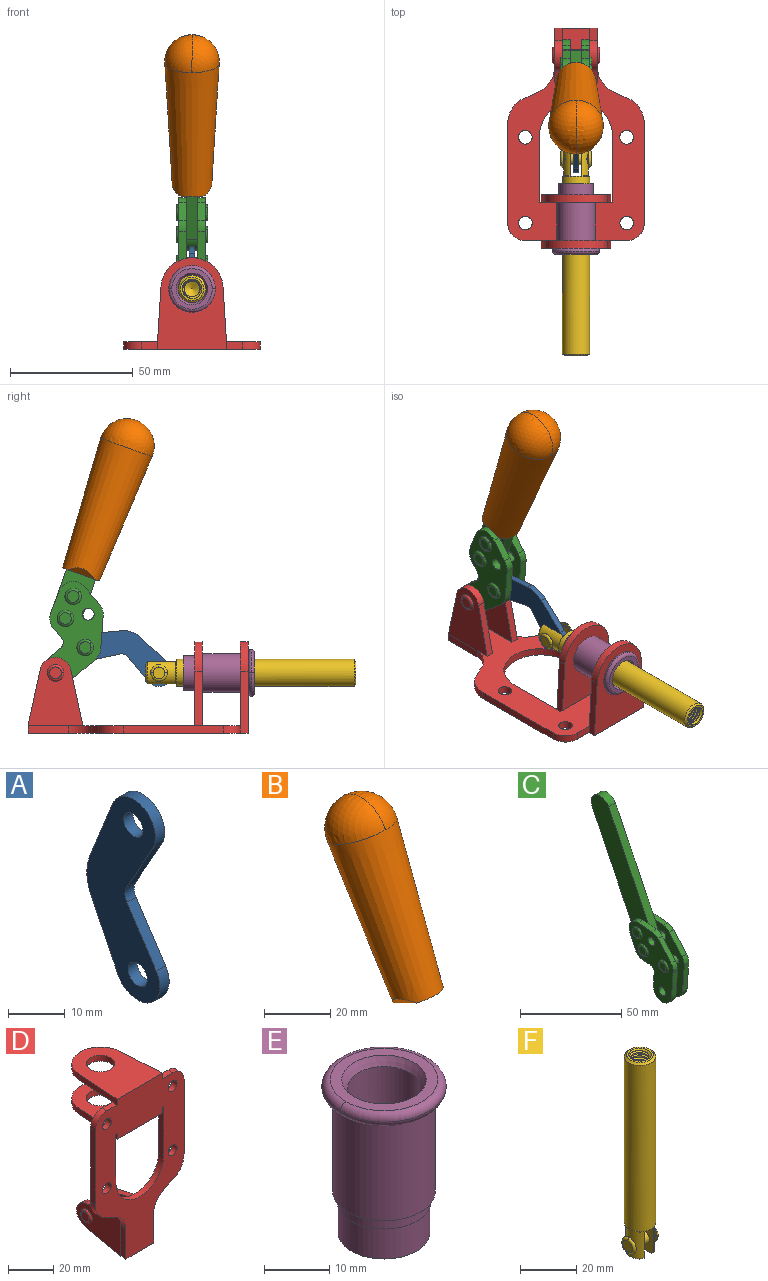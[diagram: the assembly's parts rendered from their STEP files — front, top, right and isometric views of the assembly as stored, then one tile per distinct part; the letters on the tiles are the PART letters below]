
ASSEMBLY  parts=6 mates=6
PART A: 12 faces, bbox 2.3x18.2x42.8 mm
  f0: cylinder r=2.4mm len=4.8mm, axis (1,0,0), area 34.9mm2, adj f4,f11
  f1: cylinder r=10.41mm len=8.47mm, axis (1,0,0), area 20.2mm2, adj f4,f9,f10,f11
  f2: cylinder r=3.05mm len=3.16mm, axis (1,0,0), area 7.7mm2, adj f4,f6,f7,f11
  f3: cylinder r=2.4mm len=4.8mm, axis (1,0,0), area 34.9mm2, adj f4,f11
  f4: plane 42.81x18.23mm, normal (-1,0,0), area 414.1mm2, adj f0,f1,f2,f3,f5,f6,f7,f8
  f5: cylinder r=5.54mm len=10.67mm, axis (1,0,0), area 41.8mm2, adj f4,f6,f10,f11
  f6: plane 11.66x6.53mm, normal (0,-0.87,-0.49), area 30.9mm2, adj f2,f4,f5,f11
  f7: plane 11.17x7.33mm, normal (0,-0.84,0.55), area 30.9mm2, adj f2,f4,f8,f11
  f8: cylinder r=5.54mm len=10.51mm, axis (1,0,0), area 41.8mm2, adj f4,f7,f9,f11
  f9: plane 13.67x6.67mm, normal (0,0.9,-0.44), area 35.1mm2, adj f1,f4,f8,f11
  f10: plane 14.1x5.7mm, normal (0,0.93,0.37), area 35.1mm2, adj f1,f4,f5,f11
  f11: plane 42.81x18.23mm, normal (1,0,0), area 414.1mm2, adj f0,f1,f2,f3,f5,f6,f7,f8
PART B: 11 faces, bbox 22.3x42.6x64.5 mm
  f0: sphere r=11.13mm, area 411.4mm2, adj f1,f8
  f1: cone r=11.11mm half-angle=3.3deg, axis (0,0.44,0.9), area 3251.8mm2, adj f0,f7,f8,f9,f10
  f2: cylinder r=6.16mm len=11.7mm, axis (1,0,0), area 89.5mm2, adj f3,f4,f5,f6
  f3: plane 60.23x36.75mm, normal (-1,0,0), area 763.6mm2, adj f2,f4,f6,f10
  f4: plane 51.37x25.05mm, normal (0,0.9,-0.44), area 264.2mm2, adj f2,f3,f5,f10
  f5: plane 60.23x36.75mm, normal (1,0,0), area 763.6mm2, adj f2,f4,f6,f10
  f6: plane 51.37x25.05mm, normal (0,-0.9,0.44), area 264.2mm2, adj f2,f3,f5,f10
  f7: plane 9.95x5.95mm, normal (0.71,-0.31,-0.64), area 25.8mm2, adj f1,f10
  f8: sphere r=11.13mm, area 411.4mm2, adj f0,f1
  f9: plane 9.95x5.95mm, normal (-0.71,-0.31,-0.64), area 25.8mm2, adj f1,f10
  f10: plane 14.27x11.38mm, normal (0,-0.44,-0.9), area 106.7mm2, adj f1,f3,f4,f5,f6,f7,f9
PART C: 59 faces, bbox 12.9x60.2x99.6 mm
  f0: torus R=2.39mm, axis (-1,0,0), area 14.9mm2, adj f20,f43,f51
  f1: torus R=2.39mm, axis (-1,0,0), area 14.9mm2, adj f19,f42,f51
  f2: torus R=2.39mm, axis (-1,0,0), area 14.9mm2, adj f18,f35,f51
  f3: torus R=2.39mm, axis (-1,0,0), area 14.9mm2, adj f14,f17,f23
  f4: torus R=2.39mm, axis (-1,0,0), area 14.9mm2, adj f13,f16,f23
  f5: torus R=2.39mm, axis (-1,0,0), area 14.9mm2, adj f12,f15,f23
  f6: cylinder r=2.39mm len=4.78mm, axis (1,0,0), area 46.5mm2, adj f48,f50,f51
  f7: cylinder r=2.39mm len=4.78mm, axis (1,0,0), area 46.5mm2, adj f50,f51
  f8: cylinder r=6.35mm len=12.68mm, axis (1,0,0), area 61.8mm2, adj f38,f39,f50,f51
  f9: cylinder r=2.39mm len=4.78mm, axis (-1,0,0), area 70.5mm2, adj f46,f50
  f10: cylinder r=2.39mm len=4.78mm, axis (-1,0,0), area 46.5mm2, adj f23,f45,f46
  f11: cylinder r=2.39mm len=4.78mm, axis (-1,0,0), area 46.5mm2, adj f23,f46
  f12: plane 4.78x4.78mm, normal (1,0,0), area 17.9mm2, adj f5,f15
  f13: plane 4.78x4.78mm, normal (1,0,0), area 17.9mm2, adj f4,f16
  f14: plane 4.78x4.78mm, normal (1,0,0), area 17.9mm2, adj f3,f17
  f15: torus R=2.39mm, axis (-1,0,0), area 14.9mm2, adj f5,f12,f23
  f16: torus R=2.39mm, axis (-1,0,0), area 14.9mm2, adj f4,f13,f23
  f17: torus R=2.39mm, axis (-1,0,0), area 14.9mm2, adj f3,f14,f23
  f18: plane 4.78x4.78mm, normal (-1,0,0), area 17.9mm2, adj f2,f35
  f19: plane 4.78x4.78mm, normal (-1,0,0), area 17.9mm2, adj f1,f42
  f20: plane 4.78x4.78mm, normal (-1,0,0), area 17.9mm2, adj f0,f43
  f21: plane 2.26x0.2mm, normal (1,0,0), area 0.2mm2, adj f31,f44
  f22: plane 2.26x0.2mm, normal (-1,0,0), area 0.2mm2, adj f41,f44
  f23: plane 39.37x30.77mm, normal (1,0,0), area 565.5mm2, adj f3,f4,f5,f10,f11,f15,f16,f17
  f24: cylinder r=6.1mm len=4.15mm, axis (-1,0,0), area 14.7mm2, adj f23,f25,f32,f46
  f25: plane 10.25x9.01mm, normal (0,-0.75,0.66), area 42.3mm2, adj f23,f24,f26,f46
  f26: cylinder r=6.35mm len=4.64mm, axis (-1,0,0), area 15.6mm2, adj f23,f25,f27,f46
  f27: plane 15.84x3.1mm, normal (0,-1,-0.07), area 49.2mm2, adj f23,f26,f28,f46
  f28: cylinder r=6.35mm len=12.68mm, axis (-1,0,0), area 61.8mm2, adj f23,f27,f29,f46
  f29: plane 8.11x3.1mm, normal (0,1,0.07), area 25.2mm2, adj f23,f28,f30,f46
  f30: cylinder r=3.05mm len=3.25mm, axis (-1,0,0), area 14.8mm2, adj f23,f29,f31,f46
  f31: plane 5.99x3.1mm, normal (0,0.07,-1), area 18.6mm2, adj f21,f23,f30,f44,f46
  f32: plane 9.5x3.1mm, normal (0,-0.07,1), area 29.5mm2, adj f23,f24,f33,f46,f47
  f33: cylinder r=6.1mm len=8.63mm, axis (-1,0,0), area 39.1mm2, adj f23,f32,f34,f47
  f34: plane 8.65x3.96mm, normal (0,0.91,-0.42), area 29.5mm2, adj f23,f33,f44,f47
  f35: torus R=2.39mm, axis (-1,0,0), area 14.9mm2, adj f2,f18,f51
  f36: plane 10.25x9.01mm, normal (0,-0.75,0.66), area 42.3mm2, adj f37,f49,f50,f51
  f37: cylinder r=6.35mm len=4.64mm, axis (1,0,0), area 15.6mm2, adj f36,f38,f50,f51
  f38: plane 15.84x3.1mm, normal (0,-1,-0.07), area 49.2mm2, adj f8,f37,f50,f51
  f39: plane 8.11x3.1mm, normal (0,1,0.07), area 25.2mm2, adj f8,f40,f50,f51
  f40: cylinder r=3.05mm len=3.25mm, axis (1,0,0), area 14.8mm2, adj f39,f41,f50,f51
  f41: plane 5.99x3.1mm, normal (0,0.07,-1), area 18.6mm2, adj f22,f40,f44,f50,f51
  f42: torus R=2.39mm, axis (-1,0,0), area 14.9mm2, adj f1,f19,f51
  f43: torus R=2.39mm, axis (-1,0,0), area 14.9mm2, adj f0,f20,f51
  f44: cylinder r=6.35mm len=12.12mm, axis (-1,0,0), area 128.9mm2, adj f21,f22,f23,f31,f34,f41,f46,f47
  f45: plane 2.65x1.35mm, normal (1,0,0), area 1mm2, adj f10,f55
  f46: plane 39.08x20.42mm, normal (-1,0,0), area 412.5mm2, adj f9,f10,f11,f24,f25,f26,f27,f28
  f47: plane 77.62x39.82mm, normal (1,0,0), area 850mm2, adj f32,f33,f34,f44,f53,f54,f55
  f48: plane 2.65x1.35mm, normal (-1,0,0), area 1mm2, adj f6,f55
  f49: cylinder r=6.1mm len=4.15mm, axis (1,0,0), area 14.7mm2, adj f36,f50,f51,f56
  f50: plane 39.08x20.42mm, normal (1,0,0), area 412.5mm2, adj f6,f7,f8,f9,f36,f37,f38,f39
  f51: plane 39.37x30.77mm, normal (-1,0,0), area 565.5mm2, adj f0,f1,f2,f6,f7,f8,f35,f36
  f52: plane 8.65x3.96mm, normal (0,0.91,-0.42), area 29.5mm2, adj f44,f51,f57,f58
  f53: plane 68.49x33.4mm, normal (0,0.9,-0.44), area 358.1mm2, adj f44,f47,f54,f58
  f54: cylinder r=6.35mm len=12.06mm, axis (1,0,0), area 93.7mm2, adj f47,f53,f55,f58
  f55: plane 68.49x33.4mm, normal (0,-0.9,0.44), area 358.1mm2, adj f44,f45,f46,f47,f48,f50,f54,f58
  f56: plane 9.5x3.1mm, normal (0,-0.07,1), area 29.5mm2, adj f49,f50,f51,f57,f58
  f57: cylinder r=6.1mm len=8.63mm, axis (1,0,0), area 39.1mm2, adj f51,f52,f56,f58
  f58: plane 77.62x39.82mm, normal (-1,0,0), area 850mm2, adj f44,f52,f53,f54,f55,f56,f57
PART D: 55 faces, bbox 55.7x37.4x89.8 mm
  f0: torus R=2.41mm, axis (-1,0,0), area 15mm2, adj f11,f15,f25
  f1: torus R=2.41mm, axis (-1,0,0), area 15mm2, adj f10,f12,f22
  f2: cylinder r=2.78mm len=5.56mm, axis (0,-1,0), area 54.2mm2, adj f30,f54
  f3: cylinder r=14.99mm len=29.97mm, axis (0,-1,0), area 145.9mm2, adj f30,f49,f53,f54
  f4: cylinder r=2.78mm len=5.56mm, axis (0,-1,0), area 54.2mm2, adj f30,f54
  f5: cylinder r=2.78mm len=5.56mm, axis (0,-1,0), area 54.2mm2, adj f30,f54
  f6: cylinder r=2.78mm len=5.56mm, axis (0,-1,0), area 54.2mm2, adj f30,f54
  f7: cylinder r=6.35mm len=12.7mm, axis (0,0,1), area 123.6mm2, adj f27,f51
  f8: cylinder r=6.35mm len=12.7mm, axis (0,0,-1), area 124.7mm2, adj f21,f35
  f9: cylinder r=2.41mm len=11.18mm, axis (-1,0,0), area 169.4mm2, adj f16,f19
  f10: plane 4.83x4.83mm, normal (1,0,0), area 18.3mm2, adj f1,f12
  f11: plane 4.83x4.83mm, normal (-1,0,0), area 18.3mm2, adj f0,f15
  f12: torus R=2.41mm, axis (-1,0,0), area 15mm2, adj f1,f10,f22
  f13: cylinder r=6.35mm len=12.41mm, axis (1,0,0), area 53.4mm2, adj f18,f19,f22,f23
  f14: cylinder r=6.35mm len=12.41mm, axis (-1,0,0), area 53.4mm2, adj f16,f17,f24,f25
  f15: torus R=2.41mm, axis (-1,0,0), area 15mm2, adj f0,f11,f25
  f16: plane 27.86x22.35mm, normal (1,0,0), area 425.4mm2, adj f9,f14,f17,f24,f30
  f17: plane 22.86x4.97mm, normal (0,0.21,0.98), area 72.5mm2, adj f14,f16,f25,f30
  f18: plane 22.86x4.97mm, normal (0,0.21,0.98), area 72.5mm2, adj f13,f19,f22,f30
  f19: plane 27.86x22.35mm, normal (-1,0,0), area 425.4mm2, adj f9,f13,f18,f23,f30
  f20: cylinder r=12.7mm len=25.35mm, axis (0,0,-1), area 119.8mm2, adj f21,f34,f35,f36
  f21: plane 34.21x28.07mm, normal (0,0,-1), area 702.4mm2, adj f8,f20,f30,f34,f36
  f22: plane 27.96x22.45mm, normal (1,0,0), area 407.2mm2, adj f1,f12,f13,f18,f23,f30,f42,f43
  f23: plane 22.86x4.97mm, normal (0,0.21,-0.98), area 72.5mm2, adj f13,f19,f22,f44
  f24: plane 22.86x4.97mm, normal (0,0.21,-0.98), area 72.5mm2, adj f14,f16,f25,f44
  f25: plane 27.86x22.35mm, normal (-1,0,0), area 407.1mm2, adj f0,f14,f15,f17,f24,f30,f45,f46
  f26: plane 3.1x0.95mm, normal (0,0,-1), area 2.7mm2, adj f30,f49,f50,f54
  f27: plane 34.21x28.07mm, normal (0,0,1), area 702.4mm2, adj f7,f28,f30,f50,f52
  f28: cylinder r=12.7mm len=25.35mm, axis (0,0,1), area 118.8mm2, adj f27,f50,f51,f52
  f29: plane 3.1x0.95mm, normal (0,0,-1), area 2.7mm2, adj f30,f52,f53,f54
  f30: plane 86.54x55.63mm, normal (0,1,0), area 2362.9mm2, adj f2,f3,f4,f5,f6,f16,f17,f18
  f31: plane 40.56x3.1mm, normal (-1,0,0), area 125.7mm2, adj f30,f32,f48,f54
  f32: cylinder r=7.11mm len=7.11mm, axis (0,-1,0), area 34.6mm2, adj f30,f31,f33,f54
  f33: plane 6.67x3.1mm, normal (0,0,1), area 20.4mm2, adj f30,f32,f34,f54
  f34: plane 25.39x3.13mm, normal (-1,0.06,0), area 79.5mm2, adj f20,f21,f33,f35,f54
  f35: plane 37.31x28.45mm, normal (0,0,1), area 789.9mm2, adj f8,f20,f34,f36,f54
  f36: plane 25.39x3.13mm, normal (1,0.06,0), area 79.5mm2, adj f20,f21,f35,f37,f54
  f37: plane 6.67x3.1mm, normal (0,0,1), area 20.4mm2, adj f30,f36,f38,f54
  f38: cylinder r=7.11mm len=7.11mm, axis (0,-1,0), area 34.6mm2, adj f30,f37,f39,f54
  f39: plane 40.56x3.1mm, normal (1,0,0), area 125.7mm2, adj f30,f38,f40,f54
  f40: cylinder r=11.18mm len=10.16mm, axis (0,-1,0), area 39.5mm2, adj f30,f39,f41,f54
  f41: plane 6.09x3.1mm, normal (0.42,0,-0.91), area 20.8mm2, adj f30,f40,f42,f54
  f42: cylinder r=11.18mm len=9.41mm, axis (0,-1,0), area 37.2mm2, adj f22,f30,f41,f43,f54
  f43: plane 16.5x3.1mm, normal (1,0,0), area 51.1mm2, adj f22,f42,f44,f54
  f44: plane 17.37x3.1mm, normal (0,0,-1), area 53.8mm2, adj f23,f24,f30,f43,f45,f54
  f45: plane 16.5x3.1mm, normal (-1,0,0), area 51.1mm2, adj f25,f44,f46,f54
  f46: cylinder r=11.18mm len=9.41mm, axis (0,-1,0), area 37.2mm2, adj f25,f30,f45,f47,f54
  f47: plane 6.09x3.1mm, normal (-0.42,0,-0.91), area 20.8mm2, adj f30,f46,f48,f54
  f48: cylinder r=11.18mm len=10.16mm, axis (0,-1,0), area 39.5mm2, adj f30,f31,f47,f54
  f49: plane 26.54x3.1mm, normal (-1,0,0), area 82.3mm2, adj f3,f26,f30,f54
  f50: plane 25.39x3.1mm, normal (1,0.06,0), area 78.8mm2, adj f26,f27,f28,f51,f54
  f51: plane 37.31x28.45mm, normal (0,0,-1), area 789.9mm2, adj f7,f28,f50,f52,f54
  f52: plane 25.39x3.1mm, normal (-1,0.06,0), area 78.8mm2, adj f27,f28,f29,f51,f54
  f53: plane 26.54x3.1mm, normal (1,0,0), area 82.3mm2, adj f3,f29,f30,f54
  f54: plane 89.66x55.63mm, normal (0,-1,0), area 2678.5mm2, adj f2,f3,f4,f5,f6,f26,f29,f31
PART E: 15 faces, bbox 20.6x20.6x28.7 mm
  f0: torus R=8.26mm, axis (0,0,1), area 56.8mm2, adj f1,f10,f12
  f1: torus R=8.26mm, axis (0,0,1), area 56.8mm2, adj f0,f6,f13
  f2: cylinder r=5.59mm len=25.91mm, axis (0,0,1), area 909.6mm2, adj f3,f4
  f3: cone r=6.86mm half-angle=45deg, axis (0,0,-1), area 70.2mm2, adj f2,f14
  f4: cone r=6.47mm half-angle=30deg, axis (0,0,1), area 66.7mm2, adj f2,f13
  f5: cylinder r=7.04mm len=14.07mm, axis (0,0,1), area 252.6mm2, adj f11,f14
  f6: torus R=8.26mm, axis (0,0,1), area 56.8mm2, adj f1,f12,f13
  f7: cylinder r=7.16mm len=14.33mm, axis (0,0,1), area 91.5mm2, adj f9,f11
  f8: cylinder r=7.86mm len=18.42mm, axis (0,0,1), area 909.6mm2, adj f9,f10
  f9: plane 15.72x15.72mm, normal (0,0,-1), area 33mm2, adj f7,f8
  f10: plane 16.51x16.51mm, normal (0,0,-1), area 19.9mm2, adj f0,f8,f12
  f11: plane 14.33x14.33mm, normal (0,0,-1), area 5.7mm2, adj f5,f7
  f12: torus R=8.26mm, axis (0,0,1), area 56.8mm2, adj f0,f6,f10
  f13: plane 16.51x16.51mm, normal (0,0,1), area 82.7mm2, adj f1,f4,f6
  f14: plane 14.07x14.07mm, normal (0,0,-1), area 7.8mm2, adj f3,f5
PART F: 48 faces, bbox 12.6x11.1x86.1 mm
  f0: torus R=2.41mm, axis (-1,0,0), area 15mm2, adj f30,f32,f34
  f1: torus R=2.41mm, axis (-1,0,0), area 15mm2, adj f29,f31,f33
  f2: cylinder r=5.54mm len=72.39mm, axis (0,0,1), area 2518.5mm2, adj f3,f4,f42,f43
  f3: cone r=5.54mm half-angle=45deg, axis (0,0,1), area 7.6mm2, adj f2,f5,f41
  f4: cone r=5.54mm half-angle=45deg, axis (0,0,-1), area 34.9mm2, adj f2,f39
  f5: cylinder r=5.08mm len=11.48mm, axis (0,0,1), area 108.3mm2, adj f3,f7,f8,f41
  f6: cylinder r=2.41mm len=4.83mm, axis (-1,0,0), area 71.2mm2, adj f40,f41
  f7: cylinder r=2.41mm len=4.83mm, axis (-1,0,0), area 7.6mm2, adj f5,f34
  f8: cone r=5.08mm half-angle=45deg, axis (0,0,1), area 10.6mm2, adj f5,f37,f41
  f9: cone r=3.98mm half-angle=45deg, axis (0,0,1), area 17.6mm2, adj f27,f39,f45,f46,f47
  f10: cylinder r=2.41mm len=4.83mm, axis (-1,0,0), area 7.6mm2, adj f33,f38
  f11: cylinder r=3.2mm len=6.4mm, axis (0,0,1), area 78.4mm2, adj f12,f28,f44,f45,f47
  f12: cylinder r=3.2mm len=6.4mm, axis (0,0,1), area 10.5mm2, adj f11,f13,f45,f47
  f13: cylinder r=3.2mm len=6.4mm, axis (0,0,1), area 10.5mm2, adj f12,f14,f45,f47
  f14: cylinder r=3.2mm len=6.4mm, axis (0,0,1), area 10.5mm2, adj f13,f15,f45,f47
  f15: cylinder r=3.2mm len=6.4mm, axis (0,0,1), area 10.5mm2, adj f14,f16,f45,f47
  f16: cylinder r=3.2mm len=6.4mm, axis (0,0,1), area 10.5mm2, adj f15,f17,f45,f47
  f17: cylinder r=3.2mm len=6.4mm, axis (0,0,1), area 10.5mm2, adj f16,f18,f45,f47
  f18: cylinder r=3.2mm len=6.4mm, axis (0,0,1), area 10.5mm2, adj f17,f19,f45,f47
  f19: cylinder r=3.2mm len=6.4mm, axis (0,0,1), area 10.5mm2, adj f18,f20,f45,f47
  f20: cylinder r=3.2mm len=6.4mm, axis (0,0,1), area 10.5mm2, adj f19,f21,f45,f47
  f21: cylinder r=3.2mm len=6.4mm, axis (0,0,1), area 10.5mm2, adj f20,f22,f45,f47
  f22: cylinder r=3.2mm len=6.4mm, axis (0,0,1), area 10.5mm2, adj f21,f23,f45,f47
  f23: cylinder r=3.2mm len=6.4mm, axis (0,0,1), area 10.5mm2, adj f22,f24,f45,f47
  f24: cylinder r=3.2mm len=6.4mm, axis (0,0,1), area 10.5mm2, adj f23,f25,f45,f47
  f25: cylinder r=3.2mm len=6.4mm, axis (0,0,1), area 10.5mm2, adj f24,f26,f45,f47
  f26: cylinder r=3.2mm len=6.4mm, axis (0,0,1), area 10.5mm2, adj f25,f27,f45,f47
  f27: cylinder r=3.2mm len=6.4mm, axis (0,0,1), area 7.4mm2, adj f9,f26,f45,f47
  f28: cone r=3.2mm half-angle=60deg, axis (0,0,1), area 37.2mm2, adj f11
  f29: plane 4.83x4.83mm, normal (-1,0,0), area 18.3mm2, adj f1,f31
  f30: plane 4.83x4.83mm, normal (1,0,0), area 18.3mm2, adj f0,f32
  f31: torus R=2.41mm, axis (-1,0,0), area 15mm2, adj f1,f29,f33
  f32: torus R=2.41mm, axis (-1,0,0), area 15mm2, adj f0,f30,f34
  f33: plane 6.83x6.83mm, normal (1,0,0), area 18.3mm2, adj f1,f10,f31
  f34: plane 6.83x6.83mm, normal (-1,0,0), area 18.3mm2, adj f0,f7,f32
  f35: cone r=5.08mm half-angle=45deg, axis (0,0,1), area 10.6mm2, adj f36,f38,f40
  f36: plane 7.25x1.97mm, normal (0,0,-1), area 10mm2, adj f35,f40
  f37: plane 7.25x1.97mm, normal (0,0,-1), area 10mm2, adj f8,f41
  f38: cylinder r=5.08mm len=11.48mm, axis (0,0,1), area 108.3mm2, adj f10,f35,f40,f42
  f39: plane 9.55x9.55mm, normal (0,0,1), area 22mm2, adj f4,f9
  f40: plane 12.76x10.09mm, normal (1,0,0), area 95.7mm2, adj f6,f35,f36,f38,f42,f43
  f41: plane 12.76x10.09mm, normal (-1,0,0), area 95.7mm2, adj f3,f5,f6,f8,f37,f43
  f42: cone r=5.54mm half-angle=45deg, axis (0,0,1), area 7.6mm2, adj f2,f38,f40
  f43: plane 11.07x4.7mm, normal (0,0,-1), area 50.4mm2, adj f2,f40,f41
  f44: plane 0.89x0.62mm, normal (-1,0,0), area 0.3mm2, adj f11,f45,f46,f47
  f45: bspline ~24.8x7.63mm, area 266.6mm2, adj f9,f11,f12,f13,f14,f15,f16,f17
  f46: bspline ~24.87x7.63mm, area 73.6mm2, adj f9,f44,f45,f47
  f47: bspline ~24.98x7.63mm, area 272.5mm2, adj f9,f11,f12,f13,f14,f15,f16,f17
PLACE A rot(axis=(1,0,0),110.9deg) t=(0,22.34,7.14)mm
PLACE B rot(axis=(1,0,0),45.6deg) t=(0,1.08,29.46)mm
PLACE C rot(axis=(1,0,0),45.6deg) t=(0,1.08,29.46)mm
PLACE D rot(axis=(1,0,0),90deg) t=(0,9.14,0)mm fixed
PLACE E rot(axis=(1,0,0),90deg) t=(0,9.14,0)mm
PLACE F rot(axis=(1,0,0),90deg) t=(0,14.57,0)mm
MATE revolute A.f5 <-> F.f6  axis (1,0,0) through (0,-0.9,24.61)mm
MATE fastened C.f54 <-> B.f2  axis (1,0,0) through (0,11.61,118.55)mm
MATE revolute A.f3 <-> C.f4  axis (1,0,0) through (0,29.14,34.9)mm
MATE revolute D.f0 <-> C.f7  axis (-1,0,0) through (0,41.23,24.61)mm
MATE slider F.f2 <-> D.f7  axis (0,-1,0) through (0,-44.21,24.61)mm
MATE fastened D.f7 <-> E.f0  axis (0,-1,0) through (0,-37.25,24.61)mm
